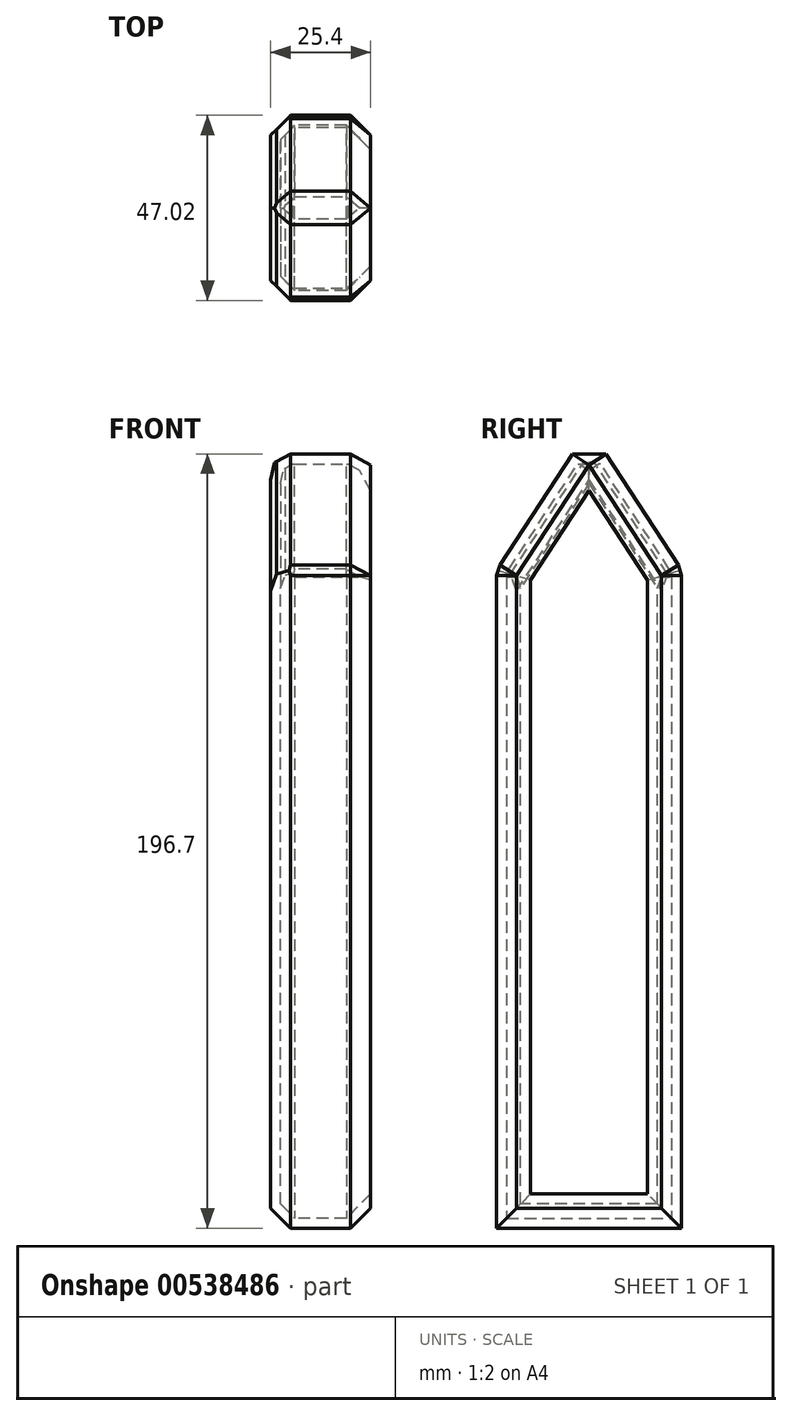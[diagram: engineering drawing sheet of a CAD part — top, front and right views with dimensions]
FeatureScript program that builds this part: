
annotation { "Feature Type Name" : "Feature", "Feature Type Description" : "" }
export const myFeature = defineFeature(function(context is Context, id is Id, definition is map)
    precondition{}
    {
        {
            var Q0;
            Q0=qCreatedBy(makeId("Right.planeOp"),FACE);
            var sketch = newSketch(context, id + "F0", { "sketchPlane" : qUnion([Q0])});
            skLineSegment(sketch, "E0.bottom", {"start": v(23.51, -101.6) * mm, "end": v(-23.51, -101.6) * mm});
            skLineSegment(sketch, "E0.left", {"start": v(23.51, -101.6) * mm, "end": v(23.51, 65.66) * mm});
            skLineSegment(sketch, "E0.right", {"start": v(-23.51, -101.6) * mm, "end": v(-23.51, 65.66) * mm});
            skPoint(sketch, "E0.middle", {"position": v(0, 0) * mm});
            skLineSegment(sketch, "E1", {"start": v(0, 101.6) * mm, "end": v(-23.51, 65.66) * mm});
            skLineSegment(sketch, "E2", {"start": v(0, 101.6) * mm, "end": v(23.51, 65.66) * mm});
            skPoint(sketch, "E3.orphan", {"position": v(-23.51, 101.6) * mm});
            skPoint(sketch, "E4.orphan", {"position": v(23.51, 101.6) * mm});
            skSolve(sketch);
        }
        {
            var Q0;
            Q0 = qSketchRegion(id + "F0", true);
            extrude(context, id + "F1", {"entities" : qUnion([Q0]), "depth" : 25.4 * mm, "offsetDistance" : 25.4 * mm, "symmetric" : true});
        }
        {
            var Q0;
            Q0=makeQuery(id+"F1.opExtrude","CAP_FACE",FACE,{"disambiguationData":[OSD([sQuery(id+"F0.wireOp",EDGE,"E0.bottom"),sQuery(id+"F0.wireOp",EDGE,"E0.left"),sQuery(id+"F0.wireOp",EDGE,"E0.right"),sQuery(id+"F0.wireOp",EDGE,"E1"),sQuery(id+"F0.wireOp",EDGE,"E2")])],"isStart":false});
            var Q1;
            Q1=makeQuery(id+"F1.opExtrude","SWEPT_FACE",FACE,{"disambiguationData":[OSD([sQuery(id+"F0.wireOp",EDGE,"E2")])]});
            var Q2;
            Q2=makeQuery(id+"F1.opExtrude","SWEPT_FACE",FACE,{"disambiguationData":[OSD([sQuery(id+"F0.wireOp",EDGE,"E1")])]});
            chamfer(context, id + "F2", {"entities" : qUnion([Q0, Q1, Q2]), "width" : 5.08 * mm, "tangentPropagation" : true});
        }
        {
            var Q0;
            Q0=makeQuery(id+"F1.opExtrude","CAP_FACE",FACE,{"disambiguationData":[OSD([sQuery(id+"F0.wireOp",EDGE,"E0.bottom"),sQuery(id+"F0.wireOp",EDGE,"E0.left"),sQuery(id+"F0.wireOp",EDGE,"E0.right"),sQuery(id+"F0.wireOp",EDGE,"E1"),sQuery(id+"F0.wireOp",EDGE,"E2")])],"isStart":true});
            chamfer(context, id + "F3", {"entities" : qUnion([Q0]), "width" : 5.08 * mm, "tangentPropagation" : true});
        }
        {
            var Q0;
            Q0=makeQuery(id+"F1.opExtrude","CAP_FACE",FACE,{"disambiguationData":[OSD([sQuery(id+"F0.wireOp",EDGE,"E0.bottom"),sQuery(id+"F0.wireOp",EDGE,"E0.left"),sQuery(id+"F0.wireOp",EDGE,"E0.right"),sQuery(id+"F0.wireOp",EDGE,"E1"),sQuery(id+"F0.wireOp",EDGE,"E2")])],"isStart":false});
            shell(context, id + "F4", {"entities" : qUnion([Q0]), "thickness" : 2.54 * mm});
        }
    });
